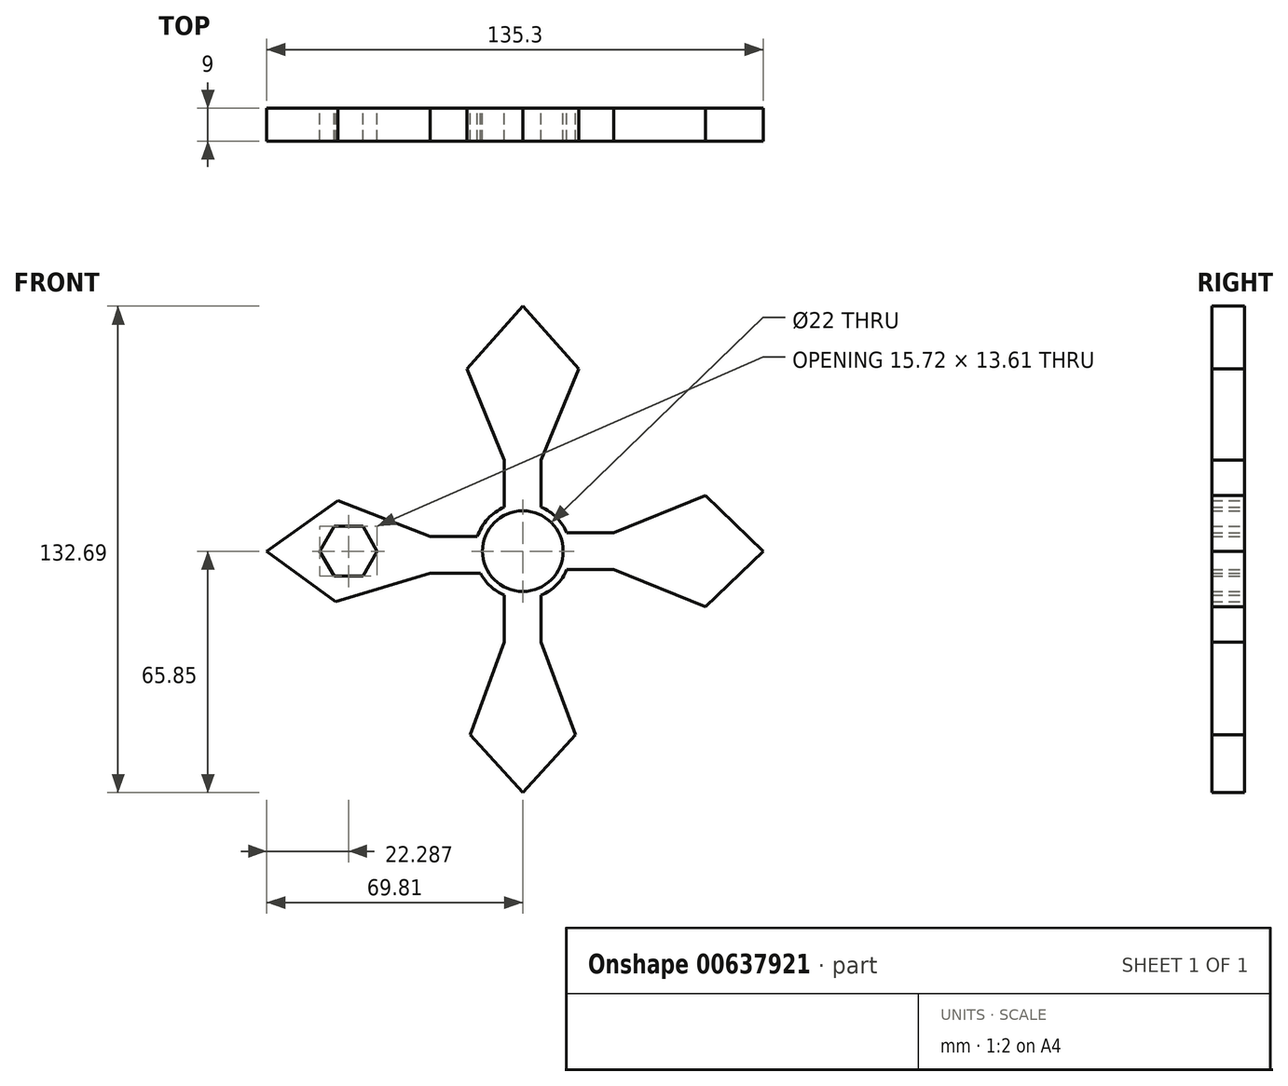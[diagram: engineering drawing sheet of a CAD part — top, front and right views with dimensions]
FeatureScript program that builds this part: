
annotation { "Feature Type Name" : "Feature", "Feature Type Description" : "" }
export const myFeature = defineFeature(function(context is Context, id is Id, definition is map)
    precondition{}
    {
        {
            var Q0;
            Q0=qCreatedBy(makeId("Front.planeOp"),FACE);
            var sketch = newSketch(context, id + "F0", { "sketchPlane" : qUnion([Q0])});
            skPoint(sketch, "E0.middle", {"position": v(0, 0) * mm});
            skCircle(sketch, "E1", {"center": v(0, 0) * mm, "radius": 11 * mm});
            skLineSegment(sketch, "E2", {"start": v(-5, -24.8) * mm, "end": v(-5, -9.8) * mm});
            skLineSegment(sketch, "E3", {"start": v(5, -24.8) * mm, "end": v(5, -9.8) * mm});
            skLineSegment(sketch, "E4", {"start": v(-5, -24.8) * mm, "end": v(-14.37, -50.12) * mm});
            skLineSegment(sketch, "E5", {"start": v(5, -24.8) * mm, "end": v(14.37, -50.12) * mm});
            skLineSegment(sketch, "E6", {"start": v(14.37, -50.12) * mm, "end": v(0, -65.85) * mm});
            skLineSegment(sketch, "E7", {"start": v(0, -65.85) * mm, "end": v(-14.37, -50.12) * mm});
            skLineSegment(sketch, "E8", {"start": v(24.8, 0) * mm, "end": v(24.8, -5) * mm});
            skLineSegment(sketch, "E9", {"start": v(24.8, -5) * mm, "end": v(24.8, 0) * mm});
            skLineSegment(sketch, "E10", {"start": v(24.8, 0) * mm, "end": v(24.8, 5) * mm});
            skLineSegment(sketch, "E11", {"start": v(24.8, 5) * mm, "end": v(9.8, 5) * mm});
            skLineSegment(sketch, "E12", {"start": v(24.8, -5) * mm, "end": v(9.8, -5) * mm});
            skLineSegment(sketch, "E13", {"start": v(24.8, -5) * mm, "end": v(49.82, -15.15) * mm});
            skLineSegment(sketch, "E14", {"start": v(24.8, 5) * mm, "end": v(49.82, 15.15) * mm});
            skLineSegment(sketch, "E15", {"start": v(49.82, 15.15) * mm, "end": v(65.5, 0) * mm});
            skLineSegment(sketch, "E16", {"start": v(49.82, -15.15) * mm, "end": v(65.5, 0) * mm});
            skLineSegment(sketch, "E17", {"start": v(-25.24, -0.97) * mm, "end": v(-25.24, 4.03) * mm});
            skLineSegment(sketch, "E18", {"start": v(-25.24, -0.97) * mm, "end": v(-25.24, -5.97) * mm});
            skLineSegment(sketch, "E19", {"start": v(0, 24.8) * mm, "end": v(5, 24.8) * mm});
            skLineSegment(sketch, "E20", {"start": v(0, 24.8) * mm, "end": v(-5, 24.8) * mm});
            skLineSegment(sketch, "E21", {"start": v(-25.24, 4.03) * mm, "end": v(-10.24, 4.03) * mm});
            skLineSegment(sketch, "E22", {"start": v(-25.24, -5.97) * mm, "end": v(-9.24, -5.97) * mm});
            skLineSegment(sketch, "E23", {"start": v(5, 24.8) * mm, "end": v(5, 9.8) * mm});
            skLineSegment(sketch, "E24", {"start": v(-5, 24.8) * mm, "end": v(-5, 9.8) * mm});
            skLineSegment(sketch, "E25", {"start": v(-25.24, -5.97) * mm, "end": v(-51.08, -13.8) * mm});
            skLineSegment(sketch, "E26", {"start": v(-25.24, 4.03) * mm, "end": v(-50.4, 13.84) * mm});
            skLineSegment(sketch, "E27", {"start": v(5, 24.8) * mm, "end": v(15.25, 49.78) * mm});
            skLineSegment(sketch, "E28", {"start": v(-5, 24.8) * mm, "end": v(-15.25, 49.78) * mm});
            skLineSegment(sketch, "E29", {"start": v(-15.25, 49.78) * mm, "end": v(0, 66.84) * mm});
            skLineSegment(sketch, "E30", {"start": v(15.25, 49.78) * mm, "end": v(0, 66.84) * mm});
            skCircle(sketch, "E31", {"center": v(0, 0) * mm, "radius": 13 * mm});
            skLineSegment(sketch, "E32", {"start": v(0, 0) * mm, "end": v(0, -65.85) * mm});
            skLineSegment(sketch, "E33", {"start": v(0, 0) * mm, "end": v(-69.81, 0) * mm});
            skLineSegment(sketch, "E34", {"start": v(-50.4, 13.84) * mm, "end": v(-69.81, 0) * mm});
            skLineSegment(sketch, "E35", {"start": v(-51.08, -13.8) * mm, "end": v(-69.81, 0) * mm});
            skLineSegment(sketch, "E36", {"start": v(0, 0) * mm, "end": v(0, 66.84) * mm});
            skLineSegment(sketch, "E37", {"start": v(0, 0) * mm, "end": v(65.5, 0) * mm});
            skLineSegment(sketch, "E38", {"start": v(-1.17, -46.48) * mm, "end": v(13.02, -46.48) * mm});
            skLineSegment(sketch, "E39", {"start": v(13.02, -46.48) * mm, "end": v(-13.02, -46.48) * mm});
            skLineSegment(sketch, "E40", {"start": v(24.8, 0) * mm, "end": v(65.5, 0) * mm});
            skLineSegment(sketch, "E41", {"start": v(-25.24, 0) * mm, "end": v(-69.81, 0) * mm});
            skLineSegment(sketch, "E42", {"start": v(-47.52, 0) * mm, "end": v(-47.52, 12.72) * mm});
            skLineSegment(sketch, "E43", {"start": v(-47.52, 12.72) * mm, "end": v(-47.52, -12.72) * mm});
            skLineSegment(sketch, "E44", {"start": v(0, 66.84) * mm, "end": v(0, 24.8) * mm});
            skLineSegment(sketch, "E45", {"start": v(13.9, 46.5) * mm, "end": v(-13.9, 46.5) * mm});
            skLineSegment(sketch, "E46", {"start": v(45.15, 0) * mm, "end": v(45.15, 13.26) * mm});
            skLineSegment(sketch, "E47", {"start": v(45.15, 13.26) * mm, "end": v(45.15, -13.26) * mm});
            skCircle(sketch, "E48.cCircle", {"center": v(-47.52, 0) * mm, "radius": 7.86 * mm, "construction": true});
            skLineSegment(sketch, "E48.0", {"start": v(-55.38, 0) * mm, "end": v(-51.45, 6.8) * mm});
            skLineSegment(sketch, "E48.1", {"start": v(-51.45, 6.8) * mm, "end": v(-43.6, 6.8) * mm});
            skLineSegment(sketch, "E48.2", {"start": v(-43.6, 6.8) * mm, "end": v(-39.66, 0) * mm});
            skLineSegment(sketch, "E48.3", {"start": v(-39.66, 0) * mm, "end": v(-43.6, -6.8) * mm});
            skLineSegment(sketch, "E48.4", {"start": v(-43.6, -6.8) * mm, "end": v(-51.45, -6.8) * mm});
            skLineSegment(sketch, "E48.5", {"start": v(-51.45, -6.8) * mm, "end": v(-55.38, 0) * mm});
            skPoint(sketch, "E49", {"position": v(0, 46.5) * mm});
            skLineSegment(sketch, "E50", {"start": v(5, -24.8) * mm, "end": v(0, -24.8) * mm});
            skLineSegment(sketch, "E51", {"start": v(-5, -24.8) * mm, "end": v(0, -24.8) * mm});
            skSolve(sketch);
        }
        {
            var Q0;
            Q0 = qSketchRegion(id + "F0", true);
            extrude(context, id + "F1", {"entities" : qUnion([Q0]), "depth" : 9 * mm, "offsetDistance" : 25 * mm});
        }
    });
